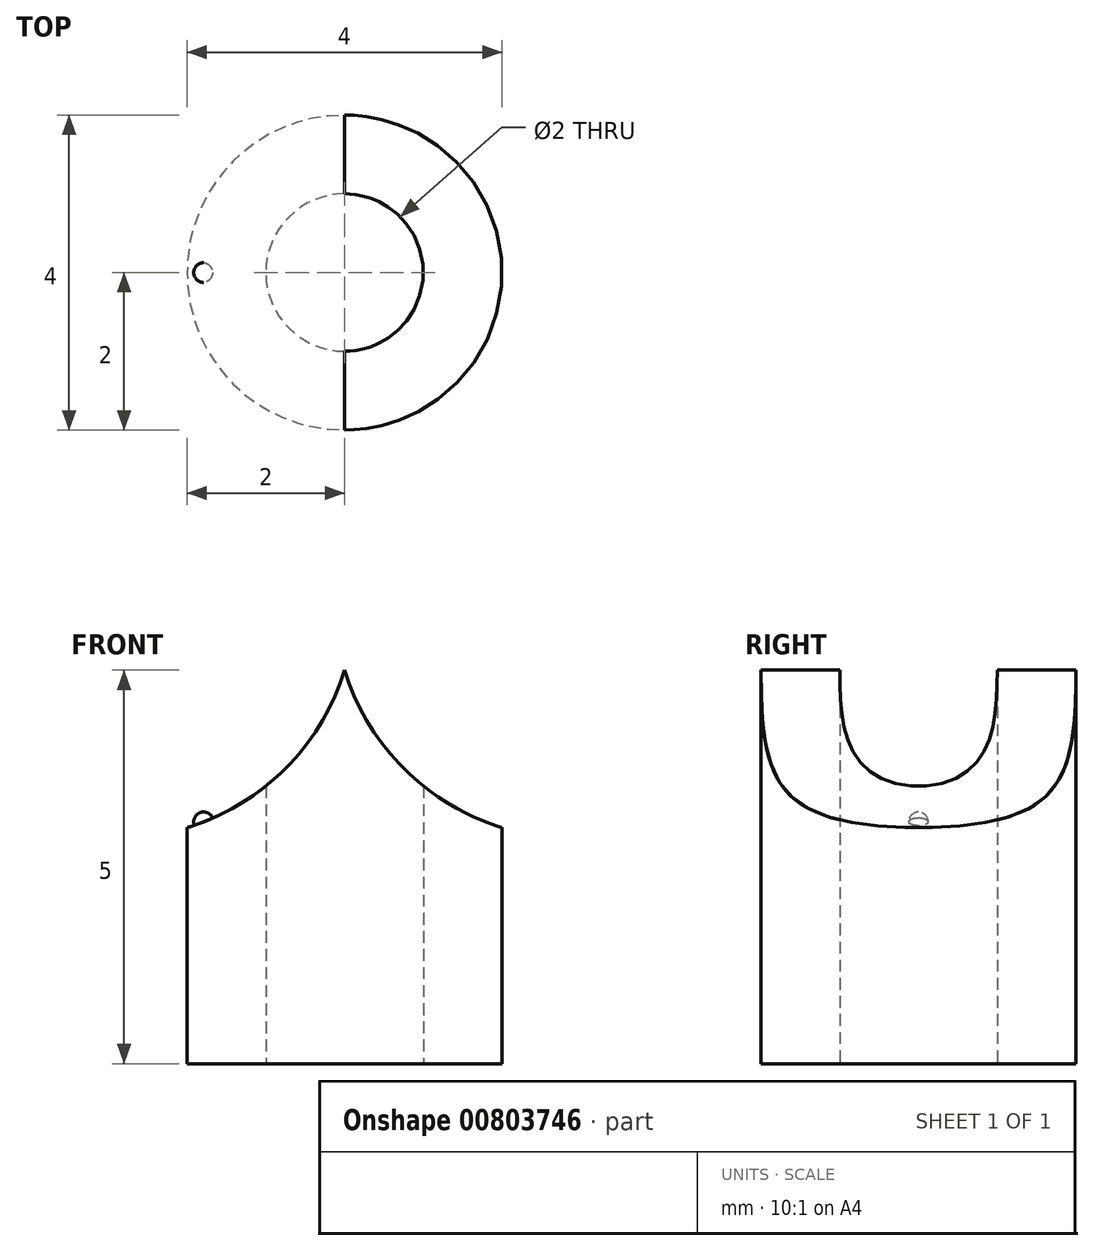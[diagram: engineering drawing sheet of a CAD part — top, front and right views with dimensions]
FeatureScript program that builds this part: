
annotation { "Feature Type Name" : "Feature", "Feature Type Description" : "" }
export const myFeature = defineFeature(function(context is Context, id is Id, definition is map)
    precondition{}
    {
        {
            var Q0;
            Q0=qCreatedBy(makeId("Top.planeOp"),FACE);
            var sketch = newSketch(context, id + "F0", { "sketchPlane" : qUnion([Q0])});
            skCircle(sketch, "E0", {"center": v(0, 0) * mm, "radius": 1 * mm});
            skCircle(sketch, "E1", {"center": v(0, 0) * mm, "radius": 2 * mm});
            skSolve(sketch);
        }
        {
            var Q0;
            Q0 = qSketchRegion(id + "F0", true);
            extrude(context, id + "F1", {"entities" : qUnion([Q0]), "depth" : 5 * mm, "offsetDistance" : 25 * mm});
        }
        {
            var Q0;
            Q0=qCreatedBy(makeId("Front.planeOp"),FACE);
            var sketch = newSketch(context, id + "F2", { "sketchPlane" : qUnion([Q0])});
            skArc(sketch, "E2", {"start": v(-2, 3) * mm, "mid": v(-0.75, 3.75) * mm, "end": v(0, 5) * mm});
            skLineSegment(sketch, "E3", {"start": v(-2, 0) * mm, "end": v(-2, 5) * mm, "construction": true});
            skLineSegment(sketch, "E4", {"start": v(2, 5) * mm, "end": v(2, 0) * mm, "construction": true});
            skArc(sketch, "E5.MirrorCS", {"start": v(2, 3) * mm, "mid": v(0.75, 3.75) * mm, "end": v(0, 5) * mm});
            skLineSegment(sketch, "E6", {"start": v(-2, 3) * mm, "end": v(-2, 5) * mm});
            skLineSegment(sketch, "E7", {"start": v(2, 5) * mm, "end": v(2, 3) * mm});
            skLineSegment(sketch, "E8", {"start": v(-2, 5) * mm, "end": v(2, 5) * mm});
            skSolve(sketch);
        }
        {
            var Q0;
            {var subQ0=sQuery(id+"F2.wireOp",EDGE,"E6");Q0=makeQuery(id+"F2.imprint","IMPRINT",FACE,{"disambiguationData":[TD([[makeQuery(id+"F2.imprint","IMPRINT",EDGE,{"derivedFrom":subQ0}),-1.0]])]});}
            var Q1;
            {var subQ0=sQuery(id+"F2.wireOp",EDGE,"E7");Q1=makeQuery(id+"F2.imprint","IMPRINT",FACE,{"disambiguationData":[TD([[makeQuery(id+"F2.imprint","IMPRINT",EDGE,{"derivedFrom":subQ0}),-1.0]])]});}
            extrude(context, id + "F3", {"entities" : qUnion([Q0, Q1]), "operationType" : NewBodyOperationType.REMOVE, "endBound" : BoundingType.SYMMETRIC, "oppositeDirection" : true, "depth" : 25 * mm, "offsetDistance" : 25 * mm});
        }
        {
            var Q0;
            Q0=qCreatedBy(makeId("Front.planeOp"),FACE);
            var sketch = newSketch(context, id + "F4", { "sketchPlane" : qUnion([Q0])});
            skCircle(sketch, "E9", {"center": v(-1.8, 3.07) * mm, "radius": 0.12 * mm});
            skLineSegment(sketch, "E10", {"start": v(-2, 0) * mm, "end": v(-2, 3) * mm});
            skLineSegment(sketch, "E11", {"start": v(2, 3) * mm, "end": v(2, 0) * mm});
            skArc(sketch, "E12.0", {"start": v(-2, 3) * mm, "mid": v(-1.95, 3.01) * mm, "end": v(-1.9, 3.03) * mm});
            skLineSegment(sketch, "E13", {"start": v(-1.8, 3.2) * mm, "end": v(-1.8, 2.95) * mm});
            skArc(sketch, "E14.trimOffspring", {"start": v(-1.68, 3.12) * mm, "mid": v(-0.63, 3.88) * mm, "end": v(0, 5) * mm});
            skSolve(sketch);
        }
        {
            var Q0;
            {var subQ2=sQuery(id+"F4.wireOp",EDGE,"E13");Q0=makeQuery(id+"F4.imprint","IMPRINT",FACE,{"disambiguationData":[TD([[makeQuery(id+"F4.imprint","IMPRINT",EDGE,{"derivedFrom":subQ2}),-1.0]])]});}
            var Q1;
            Q1=sQuery(id+"F4.wireOp",EDGE,"E13");
            revolve(context, id + "F5", {"operationType" : NewBodyOperationType.ADD, "surfaceOperationType" : NewSurfaceOperationType.NEW, "entities" : qUnion([Q0]), "axis" : qUnion([Q1]), "revolveType" : RevolveType.FULL});
        }
    });
